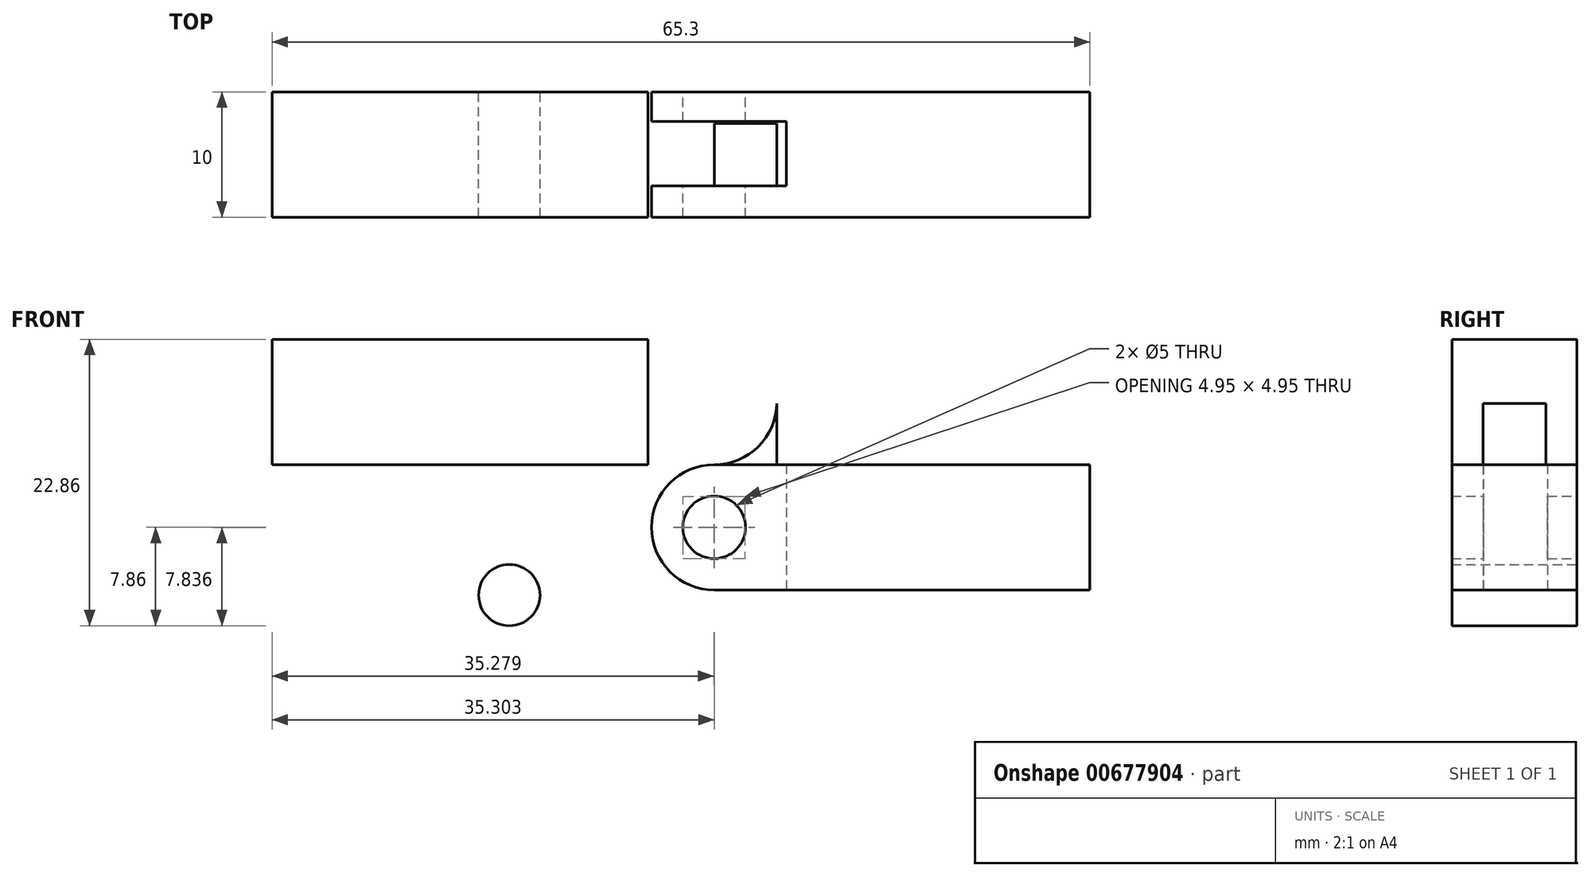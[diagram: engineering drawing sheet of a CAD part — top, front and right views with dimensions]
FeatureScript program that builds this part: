
annotation { "Feature Type Name" : "Feature", "Feature Type Description" : "" }
export const myFeature = defineFeature(function(context is Context, id is Id, definition is map)
    precondition{}
    {
        {
            var Q0;
            Q0=qCreatedBy(makeId("Front.planeOp"),FACE);
            var sketch = newSketch(context, id + "F0", { "sketchPlane" : qUnion([Q0])});
            skLineSegment(sketch, "E0.right", {"start": v(-8.17, 5) * mm, "end": v(-8.17, -5) * mm});
            skPoint(sketch, "E0.middle", {"position": v(-23.17, 0) * mm});
            skArc(sketch, "E1", {"start": v(-8.17, -5) * mm, "mid": v(-3.17, 0) * mm, "end": v(-8.17, 5) * mm});
            skCircle(sketch, "E2", {"center": v(-8.17, 0) * mm, "radius": 2.5 * mm});
            skLineSegment(sketch, "E3.bottom", {"start": v(-8.17, 5) * mm, "end": v(21.83, 5) * mm});
            skLineSegment(sketch, "E3.top", {"start": v(-8.17, -5) * mm, "end": v(21.83, -5) * mm});
            skLineSegment(sketch, "E3.right", {"start": v(21.83, 5) * mm, "end": v(21.83, -5) * mm});
            skArc(sketch, "E4", {"start": v(-8.17, 5) * mm, "mid": v(-13.17, 0) * mm, "end": v(-8.17, -5) * mm});
            skLineSegment(sketch, "E5", {"start": v(-3.17, 0) * mm, "end": v(-3.17, -5) * mm, "construction": true});
            skLineSegment(sketch, "E6", {"start": v(-3.17, -5) * mm, "end": v(-3.17, 5) * mm, "construction": true});
            skSolve(sketch);
        }
        {
            var Q0;
            Q0 = qSketchRegion(id + "F0", true);
            extrude(context, id + "F1", {"entities" : qUnion([Q0]), "depth" : 10 * mm, "offsetDistance" : 25 * mm});
        }
        {
            var Q0;
            Q0=makeQuery(id+"F1.opExtrude","SWEPT_FACE",FACE,{"disambiguationData":[OSD([sQuery(id+"F0.wireOp",EDGE,"E0.bottom"),sQuery(id+"F0.wireOp",EDGE,"E3.bottom")])]});
            var sketch = newSketch(context, id + "F2", { "sketchPlane" : qUnion([Q0])});
            skLineSegment(sketch, "E7", {"start": v(-13.47, 0) * mm, "end": v(-13.47, -2.5) * mm});
            skLineSegment(sketch, "E8", {"start": v(-13.47, -2.5) * mm, "end": v(-3.17, -2.5) * mm});
            skLineSegment(sketch, "E9", {"start": v(-3.17, -2.5) * mm, "end": v(-3.17, -7.5) * mm});
            skLineSegment(sketch, "E10", {"start": v(-3.17, -7.5) * mm, "end": v(-13.47, -7.5) * mm});
            skLineSegment(sketch, "E11", {"start": v(-13.47, -7.5) * mm, "end": v(-13.47, -10) * mm});
            skLineSegment(sketch, "E12", {"start": v(-13.47, -10) * mm, "end": v(-43.47, -10) * mm});
            skLineSegment(sketch, "E13", {"start": v(-43.47, -10) * mm, "end": v(-43.47, 0) * mm});
            skLineSegment(sketch, "E14", {"start": v(-43.47, 0) * mm, "end": v(-13.47, 0) * mm});
            skSolve(sketch);
        }
        {
            var Q0;
            Q0 = qSketchRegion(id + "F2", true);
            extrude(context, id + "F3", {"entities" : qUnion([Q0]), "operationType" : NewBodyOperationType.ADD, "depth" : 10 * mm, "offsetDistance" : 25 * mm});
        }
        {
            var Q0;
            Q0=makeQuery(id+"F3.opExtrude","SWEPT_FACE",FACE,{"disambiguationData":[OSD([sQuery(id+"F2.wireOp",EDGE,"E10")])]});
            var sketch = newSketch(context, id + "F4", { "sketchPlane" : qUnion([Q0])});
            skArc(sketch, "E15", {"start": v(-8.17, 5) * mm, "mid": v(-3.17, 10.08) * mm, "end": v(-8.32, 15) * mm});
            skLineSegment(sketch, "E16", {"start": v(-8.32, 15) * mm, "end": v(-8.32, 16.87) * mm});
            skLineSegment(sketch, "E17", {"start": v(-8.32, 16.87) * mm, "end": v(0, 16.87) * mm});
            skLineSegment(sketch, "E18", {"start": v(0, 16.87) * mm, "end": v(0, 4.76) * mm});
            skLineSegment(sketch, "E19", {"start": v(0, 4.76) * mm, "end": v(0, 3.3) * mm});
            skLineSegment(sketch, "E20", {"start": v(0, 3.3) * mm, "end": v(-8.32, 3.3) * mm});
            skLineSegment(sketch, "E21", {"start": v(-8.32, 3.3) * mm, "end": v(-8.17, 5) * mm});
            skCircle(sketch, "E22", {"center": v(-8.17, 10) * mm, "radius": 2.5 * mm});
            skSolve(sketch);
        }
        {
            var Q0;
            {var subQ1=sQuery(id+"F2.wireOp",EDGE,"E10");var subQ3=makeQuery(id+"F3.opExtrude","CAP_EDGE",EDGE,{"disambiguationData":[OSD([subQ1])],"isStart":true});var subQ4=makeQuery(id+"F3.boolean.opBoolean","SPLIT",EDGE,{"disambiguationData":[topologyDisambiguationEdgeConnected([makeQuery(id+"F1.opExtrude","SWEPT_FACE",FACE,{"disambiguationData":[OSD([sQuery(id+"F0.wireOp",EDGE,"E3.bottom")])]})])],"derivedFrom":subQ3});Q0=makeQuery(id+"F4.imprint","IMPRINT",FACE,{"disambiguationData":[TD([[makeQuery(id+"F4.imprint","IMPRINT",EDGE,{"derivedFrom":subQ4}),-1.0]])]});}
            var Q1;
            {var subQ0=sQuery(id+"F4.wireOp",EDGE,"E15");var subQ1=sQuery(id+"F2.wireOp",EDGE,"E10");var subQ4=makeQuery(id+"F3.opExtrude","CAP_EDGE",EDGE,{"disambiguationData":[OSD([subQ1])],"isStart":false});var subQ5=makeQuery(id+"F4.imprint","INTERSECT",VERTEX,{"derivedFrom":[subQ4,subQ0]});Q1=makeQuery(id+"F4.imprint","IMPRINT",FACE,{"disambiguationData":[TD([[makeQuery(id+"F4.imprint","IMPRINT",EDGE,{"disambiguationData":[TD([[subQ5,1.0]])],"derivedFrom":subQ0}),-1.0]])]});}
            extrude(context, id + "F5", {"entities" : qUnion([Q0, Q1]), "operationType" : NewBodyOperationType.REMOVE, "oppositeDirection" : true, "depth" : 10 * mm, "offsetDistance" : 25 * mm});
        }
        {
            var Q0;
            Q0=makeQuery(id+"F4.imprint","IMPRINT",FACE,{"disambiguationData":[TD([[makeQuery(id+"F4.imprint","IMPRINT",EDGE,{"derivedFrom":sQuery(id+"F4.wireOp",EDGE,"E22")}),1.0]])]});
            extrude(context, id + "F6", {"entities" : qUnion([Q0]), "operationType" : NewBodyOperationType.REMOVE, "oppositeDirection" : true, "depth" : 25 * mm, "offsetDistance" : 25 * mm});
        }
        {
            var Q0;
            Q0=qCreatedBy(makeId("Front.planeOp"),FACE);
            var sketch = newSketch(context, id + "F7", { "sketchPlane" : qUnion([Q0])});
            skCircle(sketch, "E23", {"center": v(-24.52, -5.41) * mm, "radius": 2.45 * mm});
            skSolve(sketch);
        }
        {
            var Q0;
            Q0 = qSketchRegion(id + "F7", true);
            extrude(context, id + "F8", {"entities" : qUnion([Q0]), "depth" : 10 * mm, "offsetDistance" : 25 * mm});
        }
        {
            var Q0;
            Q0=makeQuery(id+"F1.opExtrude","SWEPT_FACE",FACE,{"disambiguationData":[OSD([sQuery(id+"F0.wireOp",EDGE,"E3.top")])]});
            var sketch = newSketch(context, id + "F9", { "sketchPlane" : qUnion([Q0])});
            skLineSegment(sketch, "E24", {"start": v(-2.4, 10.9) * mm, "end": v(-13.41, 10.9) * mm});
            skLineSegment(sketch, "E25", {"start": v(-13.41, 10.9) * mm, "end": v(-13.41, 7.5) * mm});
            skLineSegment(sketch, "E26", {"start": v(-13.41, 7.5) * mm, "end": v(-2.4, 7.5) * mm});
            skLineSegment(sketch, "E27", {"start": v(-2.4, 7.5) * mm, "end": v(-2.4, 2.36) * mm});
            skLineSegment(sketch, "E28", {"start": v(-2.4, 2.36) * mm, "end": v(-13.41, 2.36) * mm});
            skLineSegment(sketch, "E29", {"start": v(-13.41, 2.36) * mm, "end": v(-13.41, -2.48) * mm});
            skLineSegment(sketch, "E30", {"start": v(-13.41, -2.48) * mm, "end": v(-2.4, -2.48) * mm});
            skLineSegment(sketch, "E31", {"start": v(-2.4, -2.48) * mm, "end": v(-2.4, -4.02) * mm});
            skLineSegment(sketch, "E32", {"start": v(-2.4, -4.02) * mm, "end": v(-16.21, -4.02) * mm});
            skLineSegment(sketch, "E33", {"start": v(-16.21, -4.02) * mm, "end": v(-16.21, 14.17) * mm});
            skLineSegment(sketch, "E34", {"start": v(-16.21, 14.17) * mm, "end": v(-2.4, 14.17) * mm});
            skLineSegment(sketch, "E35", {"start": v(-2.4, 14.17) * mm, "end": v(-2.4, 10.9) * mm});
            skSolve(sketch);
        }
        {
            var Q0;
            Q0 = qSketchRegion(id + "F9", true);
            extrude(context, id + "F10", {"entities" : qUnion([Q0]), "operationType" : NewBodyOperationType.REMOVE, "oppositeDirection" : true, "depth" : 10 * mm, "offsetDistance" : 25 * mm});
        }
    });
